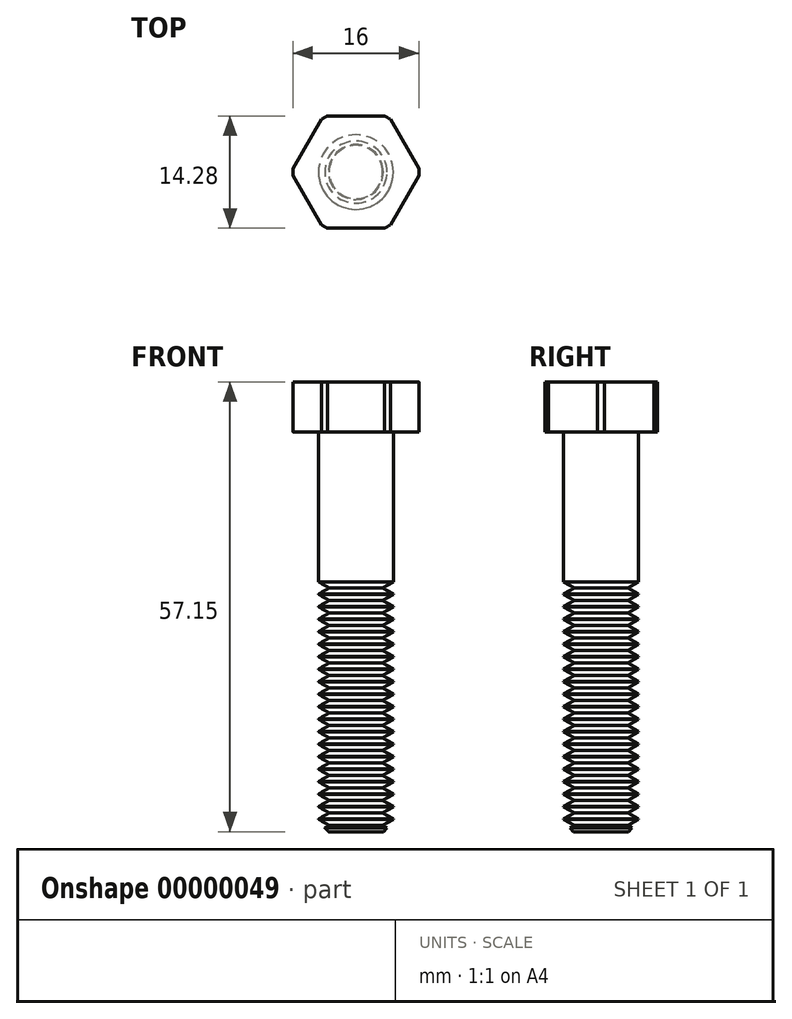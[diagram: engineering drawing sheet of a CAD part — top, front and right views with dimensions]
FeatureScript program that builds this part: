
annotation { "Feature Type Name" : "Feature", "Feature Type Description" : "" }
export const myFeature = defineFeature(function(context is Context, id is Id, definition is map)
    precondition{}
    {
        {
            var Q0;
            Q0 = qCreatedBy(makeId("Front.planeOp"), FACE);
            var sketch = newSketch(context, id + "F0", { "sketchPlane" : qUnion([Q0])});
            skLineSegment(sketch, "E0", {"start": v(0, 0) * mm, "end": v(0, 57.15) * mm});
            skLineSegment(sketch, "E1", {"start": v(0, 57.15) * mm, "end": v(8, 57.15) * mm});
            skLineSegment(sketch, "E2", {"start": v(8, 57.15) * mm, "end": v(8, 50.8) * mm});
            skLineSegment(sketch, "E3", {"start": v(8, 50.8) * mm, "end": v(4.75, 50.8) * mm});
            skLineSegment(sketch, "E4", {"start": v(4.75, 50.8) * mm, "end": v(4.75, 1.27) * mm});
            skLineSegment(sketch, "E5", {"start": v(4.75, 1.27) * mm, "end": v(3.48, 0) * mm});
            skLineSegment(sketch, "E6", {"start": v(3.48, 0) * mm, "end": v(0, 0) * mm});
            skLineSegment(sketch, "E7", {"start": v(0, 55.03) * mm, "end": v(0, 57.15) * mm, "construction": true});
            skSolve(sketch);
        }
        {
            var Q0;
            Q0=makeQuery(id+"F0.imprint","IMPRINT",FACE,{"disambiguationData":[TD([[makeQuery(id+"F0.imprint","IMPRINT",EDGE,{"derivedFrom":sQuery(id+"F0.wireOp",EDGE,"E0")}),-1.0]])]});
            var Q1;
            Q1=sQuery(id+"F0.wireOp",EDGE,"E7");
            var Q2;
            Q2=sQuery(id+"F0.wireOp",EDGE,"E7");
            revolve(context, id + "F1", {"entities" : qUnion([Q0]), "surfaceEntities" : qUnion([Q1]), "axis" : qUnion([Q2]), "revolveType" : RevolveType.FULL});
        }
        {
            var Q0;
            Q0=makeQuery(id+"F1.opRevolve","SWEPT_FACE",FACE,{"disambiguationData":[OSD([sQuery(id+"F0.wireOp",EDGE,"E1")])]});
            var sketch = newSketch(context, id + "F2", { "sketchPlane" : qUnion([Q0])});
            skLineSegment(sketch, "E8.bottom", {"start": v(-4.76, 4.76) * mm, "end": v(4.76, 4.76) * mm, "construction": true});
            skLineSegment(sketch, "E8.top", {"start": v(-4.76, -4.76) * mm, "end": v(4.76, -4.76) * mm, "construction": true});
            skLineSegment(sketch, "E8.left", {"start": v(-4.76, 4.76) * mm, "end": v(-4.76, -4.76) * mm, "construction": true});
            skLineSegment(sketch, "E8.right", {"start": v(4.76, 4.76) * mm, "end": v(4.76, -4.76) * mm, "construction": true});
            skLineSegment(sketch, "E9", {"start": v(-4.76, -4.76) * mm, "end": v(4.76, 4.76) * mm, "construction": true});
            skCircle(sketch, "E10", {"center": v(0, 0) * mm, "radius": 8 * mm});
            skLineSegment(sketch, "E11", {"start": v(-4.12, 7.14) * mm, "end": v(4.12, 7.14) * mm});
            skLineSegment(sketch, "E12", {"start": v(4.12, 7.14) * mm, "end": v(8.24, 0) * mm});
            skLineSegment(sketch, "E13", {"start": v(8.24, 0) * mm, "end": v(4.12, -7.14) * mm});
            skLineSegment(sketch, "E14", {"start": v(4.12, -7.14) * mm, "end": v(-4.12, -7.14) * mm});
            skLineSegment(sketch, "E15", {"start": v(-4.12, -7.14) * mm, "end": v(-8.24, 0) * mm});
            skLineSegment(sketch, "E16", {"start": v(-8.24, 0) * mm, "end": v(-4.12, 7.14) * mm});
            skCircle(sketch, "E17", {"center": v(0, 0) * mm, "radius": 8.24 * mm, "construction": true});
            skSolve(sketch);
        }
        {
            var Q0;
            {var subQ0=sQuery(id+"F2.wireOp",EDGE,"E11");var subQ1=sQuery(id+"F2.wireOp",EDGE,"E10");var subQ3=makeQuery(id+"F2.imprint","INTERSECT",VERTEX,{"disambiguationData":[OD(0.0)],"derivedFrom":[subQ1,subQ0]});Q0=makeQuery(id+"F2.imprint","IMPRINT",FACE,{"disambiguationData":[TD([[makeQuery(id+"F2.imprint","IMPRINT",EDGE,{"disambiguationData":[TD([[subQ3,-1.0]])],"derivedFrom":subQ1}),-1.0]])]});}
            var Q1;
            {var subQ0=sQuery(id+"F2.wireOp",EDGE,"E12");var subQ1=sQuery(id+"F2.wireOp",EDGE,"E10");var subQ3=makeQuery(id+"F2.imprint","INTERSECT",VERTEX,{"disambiguationData":[OD(0.0)],"derivedFrom":[subQ1,subQ0]});Q1=makeQuery(id+"F2.imprint","IMPRINT",FACE,{"disambiguationData":[TD([[makeQuery(id+"F2.imprint","IMPRINT",EDGE,{"disambiguationData":[TD([[subQ3,-1.0]])],"derivedFrom":subQ1}),-1.0]])]});}
            var Q2;
            {var subQ0=sQuery(id+"F2.wireOp",EDGE,"E13");var subQ1=sQuery(id+"F2.wireOp",EDGE,"E10");var subQ3=makeQuery(id+"F2.imprint","INTERSECT",VERTEX,{"disambiguationData":[OD(0.0)],"derivedFrom":[subQ1,subQ0]});Q2=makeQuery(id+"F2.imprint","IMPRINT",FACE,{"disambiguationData":[TD([[makeQuery(id+"F2.imprint","IMPRINT",EDGE,{"disambiguationData":[TD([[subQ3,-1.0]])],"derivedFrom":subQ1}),-1.0]])]});}
            var Q3;
            {var subQ0=sQuery(id+"F2.wireOp",EDGE,"E14");var subQ1=sQuery(id+"F2.wireOp",EDGE,"E10");var subQ3=makeQuery(id+"F2.imprint","INTERSECT",VERTEX,{"disambiguationData":[OD(0.0)],"derivedFrom":[subQ1,subQ0]});Q3=makeQuery(id+"F2.imprint","IMPRINT",FACE,{"disambiguationData":[TD([[makeQuery(id+"F2.imprint","IMPRINT",EDGE,{"disambiguationData":[TD([[subQ3,-1.0]])],"derivedFrom":subQ1}),-1.0]])]});}
            var Q4;
            {var subQ0=sQuery(id+"F2.wireOp",EDGE,"E15");var subQ1=sQuery(id+"F2.wireOp",EDGE,"E10");var subQ3=makeQuery(id+"F2.imprint","INTERSECT",VERTEX,{"disambiguationData":[OD(0.0)],"derivedFrom":[subQ1,subQ0]});Q4=makeQuery(id+"F2.imprint","IMPRINT",FACE,{"disambiguationData":[TD([[makeQuery(id+"F2.imprint","IMPRINT",EDGE,{"disambiguationData":[TD([[subQ3,-1.0]])],"derivedFrom":subQ1}),-1.0]])]});}
            var Q5;
            {var subQ0=sQuery(id+"F2.wireOp",EDGE,"E16");var subQ1=sQuery(id+"F2.wireOp",EDGE,"E10");var subQ3=makeQuery(id+"F2.imprint","INTERSECT",VERTEX,{"disambiguationData":[OD(0.0)],"derivedFrom":[subQ1,subQ0]});Q5=makeQuery(id+"F2.imprint","IMPRINT",FACE,{"disambiguationData":[TD([[makeQuery(id+"F2.imprint","IMPRINT",EDGE,{"disambiguationData":[TD([[subQ3,-1.0]])],"derivedFrom":subQ1}),-1.0]])]});}
            extrude(context, id + "F3", {"entities" : qUnion([Q0, Q1, Q2, Q3, Q4, Q5]), "operationType" : NewBodyOperationType.REMOVE, "oppositeDirection" : true, "depth" : 6.35 * mm});
        }
        {
            var Q0;
            Q0=qCreatedBy(makeId("Front.planeOp"),FACE);
            var sketch = newSketch(context, id + "F4", { "sketchPlane" : qUnion([Q0])});
            skLineSegment(sketch, "E18", {"start": v(4.78, 31.75) * mm, "end": v(4.78, 0) * mm, "construction": true});
            skLineSegment(sketch, "E19", {"start": v(4.78, 0) * mm, "end": v(14.94, 0) * mm});
            skLineSegment(sketch, "E20", {"start": v(14.94, 0) * mm, "end": v(14.94, 31.75) * mm});
            skLineSegment(sketch, "E21", {"start": v(14.94, 31.75) * mm, "end": v(4.78, 31.75) * mm});
            skLineSegment(sketch, "E22", {"start": v(3.4, 31.79) * mm, "end": v(3.4, 0) * mm, "construction": true});
            skLineSegment(sketch, "E23", {"start": v(4.78, 31.75) * mm, "end": v(3.4, 30.96) * mm});
            skLineSegment(sketch, "E24", {"start": v(3.4, 30.96) * mm, "end": v(4.78, 30.16) * mm});
            skLineSegment(sketch, "E25", {"start": v(4.78, 30.16) * mm, "end": v(3.4, 29.37) * mm});
            skLineSegment(sketch, "E26", {"start": v(3.4, 29.37) * mm, "end": v(4.78, 28.58) * mm});
            skLineSegment(sketch, "E27", {"start": v(4.78, 28.58) * mm, "end": v(3.4, 27.78) * mm});
            skLineSegment(sketch, "E28", {"start": v(3.4, 27.78) * mm, "end": v(4.78, 26.99) * mm});
            skLineSegment(sketch, "E29", {"start": v(4.78, 26.99) * mm, "end": v(3.4, 26.2) * mm});
            skLineSegment(sketch, "E30", {"start": v(3.4, 26.2) * mm, "end": v(4.78, 25.4) * mm});
            skLineSegment(sketch, "E31", {"start": v(4.78, 25.4) * mm, "end": v(3.4, 24.6) * mm});
            skLineSegment(sketch, "E32", {"start": v(3.4, 24.6) * mm, "end": v(4.78, 23.81) * mm});
            skLineSegment(sketch, "E33", {"start": v(4.78, 23.81) * mm, "end": v(3.4, 23.02) * mm});
            skLineSegment(sketch, "E34", {"start": v(3.4, 23.02) * mm, "end": v(4.78, 22.23) * mm});
            skLineSegment(sketch, "E35", {"start": v(4.78, 22.23) * mm, "end": v(3.4, 21.43) * mm});
            skLineSegment(sketch, "E36", {"start": v(3.4, 21.43) * mm, "end": v(4.78, 20.64) * mm});
            skLineSegment(sketch, "E37", {"start": v(4.78, 20.64) * mm, "end": v(3.4, 19.84) * mm});
            skLineSegment(sketch, "E38", {"start": v(3.4, 19.84) * mm, "end": v(4.78, 19.05) * mm});
            skLineSegment(sketch, "E39", {"start": v(4.78, 19.05) * mm, "end": v(3.4, 18.26) * mm});
            skLineSegment(sketch, "E40", {"start": v(3.4, 18.26) * mm, "end": v(4.78, 17.46) * mm});
            skLineSegment(sketch, "E41", {"start": v(4.78, 17.46) * mm, "end": v(3.4, 16.67) * mm});
            skLineSegment(sketch, "E42", {"start": v(3.4, 16.67) * mm, "end": v(4.78, 15.88) * mm});
            skLineSegment(sketch, "E43", {"start": v(4.78, 15.88) * mm, "end": v(3.4, 15.08) * mm});
            skLineSegment(sketch, "E44", {"start": v(3.4, 15.08) * mm, "end": v(4.78, 14.29) * mm});
            skLineSegment(sketch, "E45", {"start": v(4.78, 14.29) * mm, "end": v(3.4, 13.5) * mm});
            skLineSegment(sketch, "E46", {"start": v(3.4, 13.5) * mm, "end": v(4.78, 12.7) * mm});
            skLineSegment(sketch, "E47", {"start": v(4.78, 12.7) * mm, "end": v(3.4, 11.9) * mm});
            skLineSegment(sketch, "E48", {"start": v(3.4, 11.9) * mm, "end": v(4.78, 11.11) * mm});
            skLineSegment(sketch, "E49", {"start": v(4.78, 11.11) * mm, "end": v(3.4, 10.32) * mm});
            skLineSegment(sketch, "E50", {"start": v(3.4, 10.32) * mm, "end": v(4.78, 9.53) * mm});
            skLineSegment(sketch, "E51", {"start": v(4.78, 9.53) * mm, "end": v(3.4, 8.73) * mm});
            skLineSegment(sketch, "E52", {"start": v(3.4, 8.73) * mm, "end": v(4.78, 7.94) * mm});
            skLineSegment(sketch, "E53", {"start": v(4.78, 7.94) * mm, "end": v(3.4, 7.14) * mm});
            skLineSegment(sketch, "E54", {"start": v(3.4, 7.14) * mm, "end": v(4.78, 6.35) * mm});
            skLineSegment(sketch, "E55", {"start": v(4.78, 6.35) * mm, "end": v(3.4, 5.56) * mm});
            skLineSegment(sketch, "E56", {"start": v(3.4, 5.56) * mm, "end": v(4.78, 4.76) * mm});
            skLineSegment(sketch, "E57", {"start": v(4.78, 4.76) * mm, "end": v(3.4, 3.97) * mm});
            skLineSegment(sketch, "E58", {"start": v(3.4, 3.97) * mm, "end": v(4.78, 3.18) * mm});
            skLineSegment(sketch, "E59", {"start": v(4.78, 3.18) * mm, "end": v(3.4, 3.97) * mm});
            skLineSegment(sketch, "E60", {"start": v(3.4, 3.97) * mm, "end": v(4.78, 3.17) * mm});
            skLineSegment(sketch, "E61", {"start": v(4.78, 3.18) * mm, "end": v(3.4, 2.38) * mm});
            skLineSegment(sketch, "E62", {"start": v(3.4, 2.38) * mm, "end": v(4.78, 1.59) * mm});
            skLineSegment(sketch, "E63", {"start": v(4.78, 1.59) * mm, "end": v(3.4, 0.8) * mm});
            skLineSegment(sketch, "E64", {"start": v(3.4, 0.8) * mm, "end": v(4.78, 0) * mm});
            skLineSegment(sketch, "E65", {"start": v(0, 0) * mm, "end": v(0, 16.2) * mm, "construction": true});
            skSolve(sketch);
        }
        {
            var Q0;
            Q0=makeQuery(id+"F4.imprint","IMPRINT",FACE,{"disambiguationData":[TD([[makeQuery(id+"F4.imprint","IMPRINT",EDGE,{"derivedFrom":sQuery(id+"F4.wireOp",EDGE,"E19")}),1.0]])]});
            var Q1;
            Q1=sQuery(id+"F4.wireOp",EDGE,"E65");
            revolve(context, id + "F5", {"operationType" : NewBodyOperationType.REMOVE, "entities" : qUnion([Q0]), "axis" : qUnion([Q1]), "revolveType" : RevolveType.FULL});
        }
    });
